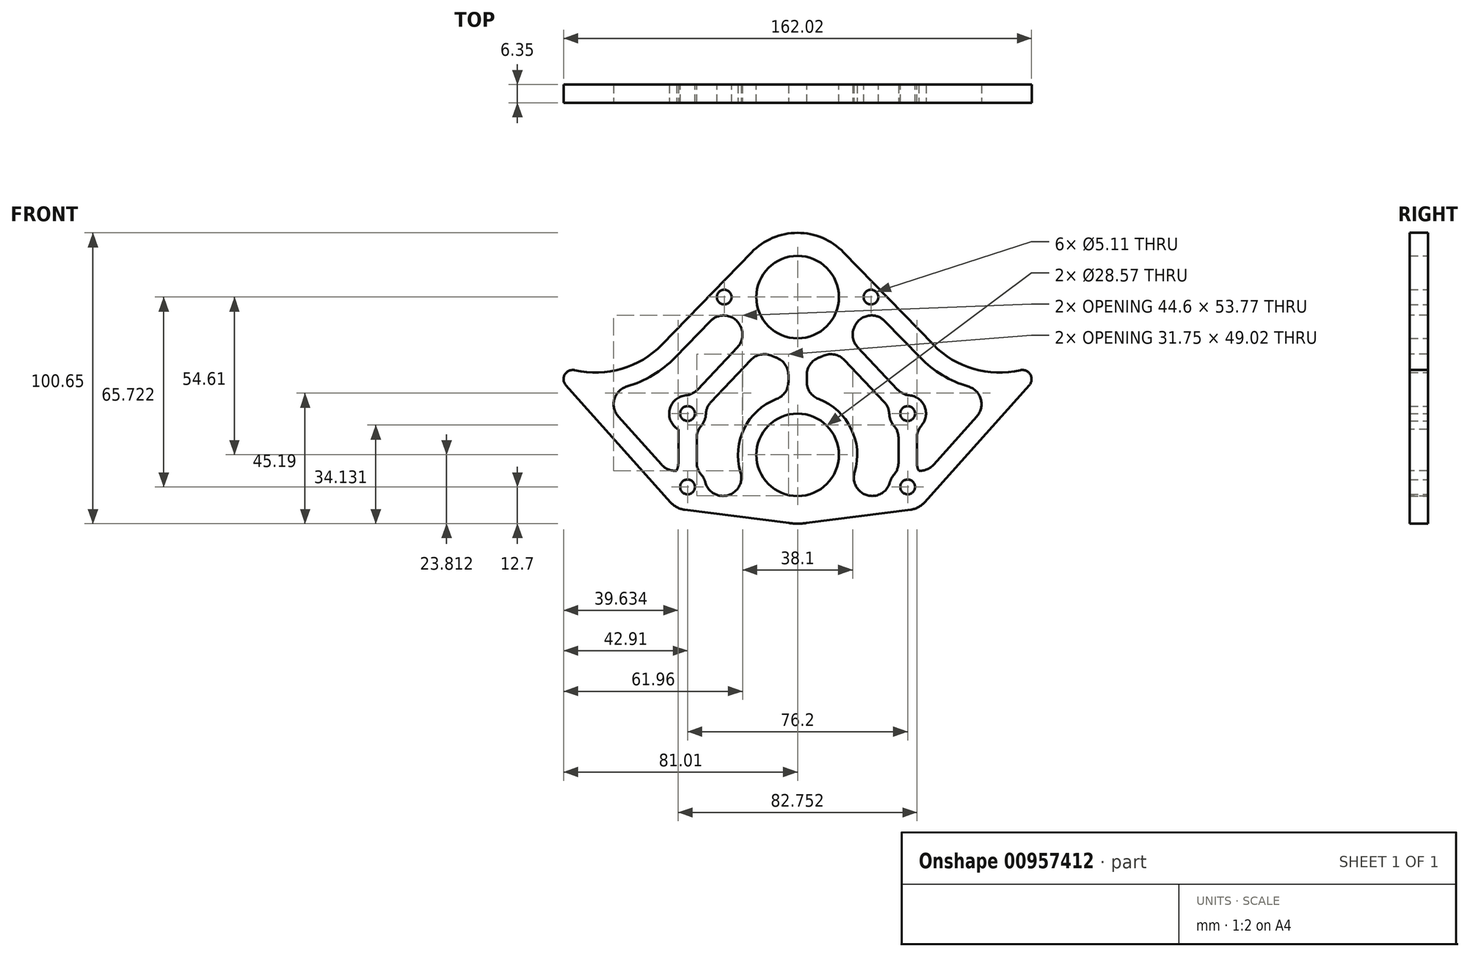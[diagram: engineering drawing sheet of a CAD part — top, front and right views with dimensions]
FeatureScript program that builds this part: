
annotation { "Feature Type Name" : "Feature", "Feature Type Description" : "" }
export const myFeature = defineFeature(function(context is Context, id is Id, definition is map)
    precondition{}
    {
        {
            var Q0;
            Q0=qCreatedBy(makeId("Front.planeOp"),FACE);
            var sketch = newSketch(context, id + "F0", { "sketchPlane" : qUnion([Q0])});
            skCircle(sketch, "E0", {"center": v(-69.85, 58.74) * mm, "radius": 31.88 * mm, "construction": true});
            skCircle(sketch, "E1", {"center": v(69.85, 58.74) * mm, "radius": 31.88 * mm, "construction": true});
            skLineSegment(sketch, "E2", {"start": v(-69.85, 58.74) * mm, "end": v(69.85, 58.74) * mm, "construction": true});
            skLineSegment(sketch, "E3", {"start": v(0, 58.74) * mm, "end": v(0, 0) * mm, "construction": true});
            skLineSegment(sketch, "E4.bottom", {"start": v(-101.6, -25.4) * mm, "end": v(101.6, -25.4) * mm, "construction": true});
            skLineSegment(sketch, "E4.top", {"start": v(-101.6, 25.4) * mm, "end": v(101.6, 25.4) * mm, "construction": true});
            skLineSegment(sketch, "E4.left", {"start": v(-101.6, -25.4) * mm, "end": v(-101.6, 25.4) * mm, "construction": true});
            skLineSegment(sketch, "E4.right", {"start": v(101.6, -25.4) * mm, "end": v(101.6, 25.4) * mm, "construction": true});
            skPoint(sketch, "E4.middle", {"position": v(0, 0) * mm});
            skCircle(sketch, "E5", {"center": v(0, -1.59) * mm, "radius": 50.8 * mm, "construction": true});
            skCircle(sketch, "E6", {"center": v(-69.85, 58.74) * mm, "radius": 7.62 * mm, "construction": true});
            skCircle(sketch, "E7", {"center": v(69.85, 58.74) * mm, "radius": 7.62 * mm, "construction": true});
            skCircle(sketch, "E8", {"center": v(0, 53.02) * mm, "radius": 38.1 * mm, "construction": true});
            skCircle(sketch, "E9", {"center": v(0, 53.02) * mm, "radius": 27.94 * mm, "construction": true});
            skCircle(sketch, "E10", {"center": v(0, -1.59) * mm, "radius": 26.67 * mm, "construction": true});
            skCircle(sketch, "E11", {"center": v(0, 53.02) * mm, "radius": 19.05 * mm, "construction": true});
            skCircle(sketch, "E12", {"center": v(0, -1.59) * mm, "radius": 35.56 * mm, "construction": true});
            skCircle(sketch, "E13", {"center": v(-69.85, 58.74) * mm, "radius": 8.9 * mm, "construction": true});
            skCircle(sketch, "E14", {"center": v(69.85, 58.74) * mm, "radius": 8.9 * mm, "construction": true});
            skCircle(sketch, "E15", {"center": v(0, 53.02) * mm, "radius": 14.29 * mm});
            skCircle(sketch, "E16", {"center": v(0, -1.59) * mm, "radius": 14.29 * mm});
            skCircle(sketch, "E17", {"center": v(-88.9, 12.7) * mm, "radius": 2.55 * mm, "construction": true});
            skCircle(sketch, "E18.0.1.0", {"center": v(-88.9, -12.7) * mm, "radius": 2.55 * mm, "construction": true});
            skCircle(sketch, "E18.1.0.0", {"center": v(-63.5, 12.7) * mm, "radius": 2.55 * mm, "construction": true});
            skCircle(sketch, "E18.1.1.0", {"center": v(-63.5, -12.7) * mm, "radius": 2.55 * mm, "construction": true});
            skCircle(sketch, "E18.2.0.0", {"center": v(-38.1, 12.7) * mm, "radius": 2.55 * mm});
            skCircle(sketch, "E18.2.1.0", {"center": v(-38.1, -12.7) * mm, "radius": 2.55 * mm});
            skCircle(sketch, "E18.3.0.0", {"center": v(-12.7, 12.7) * mm, "radius": 2.55 * mm, "construction": true});
            skCircle(sketch, "E18.3.1.0", {"center": v(-12.7, -12.7) * mm, "radius": 2.55 * mm, "construction": true});
            skCircle(sketch, "E18.4.0.0", {"center": v(12.7, 12.7) * mm, "radius": 2.55 * mm, "construction": true});
            skCircle(sketch, "E18.4.1.0", {"center": v(12.7, -12.7) * mm, "radius": 2.55 * mm, "construction": true});
            skCircle(sketch, "E18.5.0.0", {"center": v(38.1, 12.7) * mm, "radius": 2.55 * mm});
            skCircle(sketch, "E18.5.1.0", {"center": v(38.1, -12.7) * mm, "radius": 2.55 * mm});
            skCircle(sketch, "E18.6.0.0", {"center": v(63.5, 12.7) * mm, "radius": 2.55 * mm, "construction": true});
            skCircle(sketch, "E18.6.1.0", {"center": v(63.5, -12.7) * mm, "radius": 2.55 * mm, "construction": true});
            skCircle(sketch, "E18.7.0.0", {"center": v(88.9, 12.7) * mm, "radius": 2.55 * mm, "construction": true});
            skCircle(sketch, "E18.7.1.0", {"center": v(88.9, -12.7) * mm, "radius": 2.55 * mm, "construction": true});
            skLineSegment(sketch, "E18.direction1", {"start": v(-88.9, 12.7) * mm, "end": v(-63.5, 12.7) * mm, "construction": true});
            skLineSegment(sketch, "E18.direction2", {"start": v(-88.9, 12.7) * mm, "end": v(-88.9, -12.7) * mm, "construction": true});
            skArc(sketch, "E19", {"start": v(-93.62, 37.5) * mm, "mid": v(-98.95, 71.76) * mm, "end": v(-69.85, 90.61) * mm, "construction": true});
            skLineSegment(sketch, "E20", {"start": v(-69.85, 90.61) * mm, "end": v(69.85, 90.61) * mm, "construction": true});
            skArc(sketch, "E21", {"start": v(69.85, 90.61) * mm, "mid": v(98.95, 71.76) * mm, "end": v(93.62, 37.5) * mm, "construction": true});
            skCircle(sketch, "E22", {"center": v(-69.85, 58.74) * mm, "radius": 9.55 * mm, "construction": true});
            skCircle(sketch, "E23", {"center": v(69.85, 58.74) * mm, "radius": 9.55 * mm, "construction": true});
            skLineSegment(sketch, "E24", {"start": v(-67.64, 84.04) * mm, "end": v(-69.85, 58.74) * mm, "construction": true});
            skLineSegment(sketch, "E25", {"start": v(-69.85, 58.74) * mm, "end": v(-72.06, 33.43) * mm, "construction": true});
            skCircle(sketch, "E26", {"center": v(-72.06, 33.43) * mm, "radius": 2.55 * mm, "construction": true});
            skCircle(sketch, "E27", {"center": v(-67.64, 84.04) * mm, "radius": 2.55 * mm, "construction": true});
            skCircle(sketch, "E28.MirrorC", {"center": v(72.06, 33.43) * mm, "radius": 2.55 * mm, "construction": true});
            skLineSegment(sketch, "E29.MirrorCS", {"start": v(69.85, 58.74) * mm, "end": v(72.06, 33.43) * mm, "construction": true});
            skLineSegment(sketch, "E30.MirrorCS", {"start": v(67.64, 84.04) * mm, "end": v(69.85, 58.74) * mm, "construction": true});
            skCircle(sketch, "E31.MirrorC", {"center": v(67.64, 84.04) * mm, "radius": 2.55 * mm, "construction": true});
            skCircle(sketch, "E32", {"center": v(0, -1.59) * mm, "radius": 23.81 * mm, "construction": true});
            skArc(sketch, "E33", {"start": v(3.03, -25.2) * mm, "mid": v(0, -25.4) * mm, "end": v(-3.03, -25.2) * mm});
            skCircle(sketch, "E34", {"center": v(-38.1, -12.7) * mm, "radius": 7.94 * mm, "construction": true});
            skCircle(sketch, "E35", {"center": v(38.1, -12.7) * mm, "radius": 7.94 * mm, "construction": true});
            skLineSegment(sketch, "E36", {"start": v(-3.03, -25.2) * mm, "end": v(-39.11, -20.57) * mm});
            skArc(sketch, "E37", {"start": v(-39.11, -20.57) * mm, "mid": v(-41.8, -19.72) * mm, "end": v(-44.02, -18) * mm});
            skLineSegment(sketch, "E38", {"start": v(-44.02, -18) * mm, "end": v(-80.2, 22.5) * mm});
            skLineSegment(sketch, "E39", {"start": v(3.03, -25.2) * mm, "end": v(39.11, -20.57) * mm});
            skArc(sketch, "E40", {"start": v(39.11, -20.57) * mm, "mid": v(41.8, -19.72) * mm, "end": v(44.02, -18) * mm});
            skLineSegment(sketch, "E41", {"start": v(44.02, -18) * mm, "end": v(80.2, 22.5) * mm});
            skCircle(sketch, "E42", {"center": v(-51.03, 75.8) * mm, "radius": 17.78 * mm, "construction": true});
            skCircle(sketch, "E43", {"center": v(-53.69, 37.52) * mm, "radius": 17.78 * mm, "construction": true});
            skCircle(sketch, "E44", {"center": v(51.03, 75.8) * mm, "radius": 17.78 * mm, "construction": true});
            skCircle(sketch, "E45", {"center": v(53.69, 37.52) * mm, "radius": 17.78 * mm, "construction": true});
            skCircle(sketch, "E46", {"center": v(-51.03, 75.8) * mm, "radius": 11.11 * mm, "construction": true});
            skCircle(sketch, "E47", {"center": v(-53.69, 37.52) * mm, "radius": 11.11 * mm, "construction": true});
            skCircle(sketch, "E48", {"center": v(53.69, 37.52) * mm, "radius": 11.11 * mm, "construction": true});
            skCircle(sketch, "E49", {"center": v(51.03, 75.8) * mm, "radius": 11.11 * mm, "construction": true});
            skCircle(sketch, "E50", {"center": v(0, 53.02) * mm, "radius": 22.23 * mm, "construction": true});
            skArc(sketch, "E51", {"start": v(-77.12, 27.7) * mm, "mid": v(-60.88, 28.15) * mm, "end": v(-46.98, 36.54) * mm});
            skLineSegment(sketch, "E52", {"start": v(-46.98, 36.54) * mm, "end": v(-15.95, 68.5) * mm});
            skArc(sketch, "E53", {"start": v(15.95, 68.5) * mm, "mid": v(0, 75.25) * mm, "end": v(-15.95, 68.5) * mm});
            skArc(sketch, "E54", {"start": v(46.98, 36.54) * mm, "mid": v(60.88, 28.15) * mm, "end": v(77.12, 27.7) * mm});
            skLineSegment(sketch, "E55", {"start": v(46.98, 36.54) * mm, "end": v(15.95, 68.5) * mm});
            skPoint(sketch, "E56.visualSharp", {"position": v(-93.62, 37.5) * mm});
            skArc(sketch, "E56.filletArc", {"start": v(-77.12, 27.7) * mm, "mid": v(-80.57, 26.23) * mm, "end": v(-80.2, 22.5) * mm});
            skPoint(sketch, "E57.visualSharp", {"position": v(93.62, 37.5) * mm});
            skArc(sketch, "E57.filletArc", {"start": v(80.2, 22.5) * mm, "mid": v(80.57, 26.23) * mm, "end": v(77.12, 27.7) * mm});
            skLineSegment(sketch, "E58", {"start": v(25.4, 53.02) * mm, "end": v(0, 53.02) * mm, "construction": true});
            skLineSegment(sketch, "E59", {"start": v(0, 53.02) * mm, "end": v(-25.4, 53.02) * mm, "construction": true});
            skCircle(sketch, "E60", {"center": v(-25.4, 53.02) * mm, "radius": 2.55 * mm});
            skCircle(sketch, "E61", {"center": v(25.4, 53.02) * mm, "radius": 2.55 * mm});
            skSolve(sketch);
        }
        {
            var Q0;
            Q0=qSketchRegion(id+"F0",true);
            extrude(context, id + "F1", {"entities" : qUnion([Q0]), "depth" : 6.35 * mm, "offsetDistance" : 25.4 * mm});
        }
        {
            var Q0;
            Q0=makeQuery(id+"F1.opExtrude","CAP_FACE",FACE,{"disambiguationData":[OSD([sQuery(id+"F0.wireOp",EDGE,"E15"),sQuery(id+"F0.wireOp",EDGE,"E16"),sQuery(id+"F0.wireOp",EDGE,"E18.2.0.0"),sQuery(id+"F0.wireOp",EDGE,"E18.2.1.0"),sQuery(id+"F0.wireOp",EDGE,"E18.5.0.0"),sQuery(id+"F0.wireOp",EDGE,"E18.5.1.0"),sQuery(id+"F0.wireOp",EDGE,"E33"),sQuery(id+"F0.wireOp",EDGE,"E36"),sQuery(id+"F0.wireOp",EDGE,"E37"),sQuery(id+"F0.wireOp",EDGE,"E38"),sQuery(id+"F0.wireOp",EDGE,"E39"),sQuery(id+"F0.wireOp",EDGE,"E40"),sQuery(id+"F0.wireOp",EDGE,"E41"),sQuery(id+"F0.wireOp",EDGE,"E51"),sQuery(id+"F0.wireOp",EDGE,"E52"),sQuery(id+"F0.wireOp",EDGE,"E53"),sQuery(id+"F0.wireOp",EDGE,"E54"),sQuery(id+"F0.wireOp",EDGE,"E55"),sQuery(id+"F0.wireOp",EDGE,"E56.filletArc"),sQuery(id+"F0.wireOp",EDGE,"E57.filletArc"),sQuery(id+"F0.wireOp",EDGE,"E60"),sQuery(id+"F0.wireOp",EDGE,"E61")])],"isStart":false});
            var sketch = newSketch(context, id + "F2", { "sketchPlane" : qUnion([Q0])});
            skCircle(sketch, "E62", {"center": v(0, 53.02) * mm, "radius": 22.23 * mm, "construction": true});
            skCircle(sketch, "E63", {"center": v(25.4, 53.02) * mm, "radius": 6.35 * mm, "construction": true});
            skCircle(sketch, "E64", {"center": v(-25.4, 53.02) * mm, "radius": 6.35 * mm, "construction": true});
            skCircle(sketch, "E65", {"center": v(-38.1, 12.7) * mm, "radius": 6.35 * mm, "construction": true});
            skCircle(sketch, "E66", {"center": v(-38.1, -12.7) * mm, "radius": 6.35 * mm, "construction": true});
            skCircle(sketch, "E67", {"center": v(38.1, -12.7) * mm, "radius": 6.35 * mm, "construction": true});
            skCircle(sketch, "E68", {"center": v(38.1, 12.7) * mm, "radius": 6.35 * mm, "construction": true});
            skLineSegment(sketch, "E69", {"start": v(-38.1, -12.7) * mm, "end": v(-38.1, 12.7) * mm, "construction": true});
            skLineSegment(sketch, "E70", {"start": v(-41.27, -7.2) * mm, "end": v(-41.27, 7.2) * mm});
            skLineSegment(sketch, "E71", {"start": v(-34.92, -7.2) * mm, "end": v(-34.92, 7.2) * mm});
            skCircle(sketch, "E72", {"center": v(0, -1.59) * mm, "radius": 20.64 * mm, "construction": true});
            skLineSegment(sketch, "E73", {"start": v(0, -1.59) * mm, "end": v(0, 53.02) * mm, "construction": true});
            skLineSegment(sketch, "E74", {"start": v(-3.18, 18.8) * mm, "end": v(-3.18, 31.03) * mm});
            skLineSegment(sketch, "E75", {"start": v(0, 53.02) * mm, "end": v(-38.1, 12.7) * mm, "construction": true});
            skLineSegment(sketch, "E76", {"start": v(-32.02, 14.52) * mm, "end": v(-12.8, 34.85) * mm});
            skArc(sketch, "E77.0", {"start": v(-38.3, -14.27) * mm, "mid": v(-38.84, -14.1) * mm, "end": v(-39.28, -13.76) * mm, "construction": true});
            skLineSegment(sketch, "E77.1", {"start": v(42.42, 32.11) * mm, "end": v(11.4, 64.08) * mm, "construction": true});
            skArc(sketch, "E77.2", {"start": v(11.4, 64.08) * mm, "mid": v(0, 68.9) * mm, "end": v(-11.4, 64.08) * mm, "construction": true});
            skLineSegment(sketch, "E77.3", {"start": v(-42.42, 32.11) * mm, "end": v(-11.4, 64.08) * mm, "construction": true});
            skArc(sketch, "E77.4", {"start": v(-69.92, 20.51) * mm, "mid": v(-54.99, 23.52) * mm, "end": v(-42.42, 32.11) * mm});
            skArc(sketch, "E77.5", {"start": v(42.42, 32.11) * mm, "mid": v(54.99, 23.52) * mm, "end": v(69.92, 20.51) * mm, "construction": true});
            skLineSegment(sketch, "E77.6", {"start": v(-39.28, -13.76) * mm, "end": v(-69.92, 20.51) * mm, "construction": true});
            skLineSegment(sketch, "E77.7", {"start": v(39.28, -13.76) * mm, "end": v(69.92, 20.51) * mm, "construction": true});
            skArc(sketch, "E77.8", {"start": v(38.3, -14.27) * mm, "mid": v(38.84, -14.1) * mm, "end": v(39.28, -13.76) * mm, "construction": true});
            skLineSegment(sketch, "E77.9", {"start": v(2.22, -18.9) * mm, "end": v(38.3, -14.27) * mm, "construction": true});
            skArc(sketch, "E77.10", {"start": v(2.22, -18.9) * mm, "mid": v(0, -19.05) * mm, "end": v(-2.22, -18.9) * mm, "construction": true});
            skLineSegment(sketch, "E77.11", {"start": v(-2.22, -18.9) * mm, "end": v(-38.3, -14.27) * mm, "construction": true});
            skArc(sketch, "E78", {"start": v(-32.2, -15.06) * mm, "mid": v(-32.1, -10.62) * mm, "end": v(-34.92, -7.2) * mm});
            skArc(sketch, "E79", {"start": v(-3.18, 18.8) * mm, "mid": v(-19.9, 3.87) * mm, "end": v(-13.13, -17.5) * mm});
            skLineSegment(sketch, "E80", {"start": v(-13.13, -17.5) * mm, "end": v(-32.2, -15.06) * mm});
            skArc(sketch, "E81", {"start": v(-32.02, 14.52) * mm, "mid": v(-32.2, 10.35) * mm, "end": v(-34.92, 7.2) * mm});
            skArc(sketch, "E82", {"start": v(-12.8, 34.85) * mm, "mid": v(-8.21, 32.37) * mm, "end": v(-3.17, 31.03) * mm});
            skLineSegment(sketch, "E83", {"start": v(-36.63, 18.88) * mm, "end": v(-17.42, 39.21) * mm});
            skArc(sketch, "E84", {"start": v(-41.27, 7.2) * mm, "mid": v(-44, 15.05) * mm, "end": v(-36.63, 18.88) * mm});
            skArc(sketch, "E85", {"start": v(-17.42, 39.21) * mm, "mid": v(-20, 43.33) * mm, "end": v(-21.63, 47.91) * mm});
            skArc(sketch, "E86", {"start": v(-27.82, 47.15) * mm, "mid": v(-24.63, 46.72) * mm, "end": v(-21.63, 47.91) * mm});
            skLineSegment(sketch, "E87", {"start": v(-42.42, 32.11) * mm, "end": v(-27.82, 47.15) * mm});
            skLineSegment(sketch, "E88", {"start": v(-43.38, -9.17) * mm, "end": v(-69.92, 20.51) * mm});
            skArc(sketch, "E89", {"start": v(-41.27, -7.2) * mm, "mid": v(-42.44, -8.07) * mm, "end": v(-43.38, -9.17) * mm});
            skArc(sketch, "E90.MirrorCS", {"start": v(41.27, -7.2) * mm, "mid": v(42.44, -8.07) * mm, "end": v(43.38, -9.17) * mm});
            skArc(sketch, "E91.MirrorCS", {"start": v(27.82, 47.15) * mm, "mid": v(24.63, 46.72) * mm, "end": v(21.63, 47.91) * mm});
            skArc(sketch, "E92.MirrorCS", {"start": v(32.2, -15.06) * mm, "mid": v(32.1, -10.62) * mm, "end": v(34.92, -7.2) * mm});
            skLineSegment(sketch, "E93.MirrorCS", {"start": v(13.13, -17.5) * mm, "end": v(32.2, -15.06) * mm});
            skLineSegment(sketch, "E94.MirrorCS", {"start": v(43.38, -9.17) * mm, "end": v(69.92, 20.51) * mm});
            skArc(sketch, "E95.MirrorCS", {"start": v(41.27, 7.2) * mm, "mid": v(44, 15.05) * mm, "end": v(36.63, 18.88) * mm});
            skArc(sketch, "E96.MirrorCS", {"start": v(32.02, 14.52) * mm, "mid": v(32.2, 10.35) * mm, "end": v(34.92, 7.2) * mm});
            skLineSegment(sketch, "E97.MirrorCS", {"start": v(42.42, 32.11) * mm, "end": v(27.82, 47.15) * mm});
            skLineSegment(sketch, "E98.MirrorCS", {"start": v(32.02, 14.52) * mm, "end": v(12.8, 34.85) * mm});
            skLineSegment(sketch, "E99.MirrorCS", {"start": v(3.18, 18.8) * mm, "end": v(3.18, 31.03) * mm});
            skArc(sketch, "E100.MirrorCS", {"start": v(69.92, 20.51) * mm, "mid": v(54.99, 23.52) * mm, "end": v(42.42, 32.11) * mm});
            skLineSegment(sketch, "E101.MirrorCS", {"start": v(41.27, -7.2) * mm, "end": v(41.27, 7.2) * mm});
            skLineSegment(sketch, "E102.MirrorCS", {"start": v(0, 53.02) * mm, "end": v(38.1, 12.7) * mm, "construction": true});
            skLineSegment(sketch, "E103.MirrorCS", {"start": v(34.92, -7.2) * mm, "end": v(34.92, 7.2) * mm});
            skArc(sketch, "E104.MirrorCS", {"start": v(17.42, 39.21) * mm, "mid": v(20, 43.33) * mm, "end": v(21.63, 47.91) * mm});
            skArc(sketch, "E105.MirrorCS", {"start": v(-2.22, -18.9) * mm, "mid": v(0, -19.05) * mm, "end": v(2.22, -18.9) * mm, "construction": true});
            skArc(sketch, "E106.MirrorCS", {"start": v(3.18, 18.8) * mm, "mid": v(19.9, 3.87) * mm, "end": v(13.13, -17.5) * mm});
            skLineSegment(sketch, "E107.MirrorCS", {"start": v(38.1, -12.7) * mm, "end": v(38.1, 12.7) * mm, "construction": true});
            skArc(sketch, "E108.MirrorCS", {"start": v(12.8, 34.85) * mm, "mid": v(8.21, 32.37) * mm, "end": v(3.17, 31.03) * mm});
            skLineSegment(sketch, "E109.MirrorCS", {"start": v(36.63, 18.88) * mm, "end": v(17.42, 39.21) * mm});
            skSolve(sketch);
        }
        {
            var Q0;
            Q0 = qSketchRegion(id + "F2", true);
            extrude(context, id + "F3", {"entities" : qUnion([Q0]), "operationType" : NewBodyOperationType.REMOVE, "oppositeDirection" : true, "depth" : 25.4 * mm, "offsetDistance" : 25.4 * mm});
        }
        {
            var Q0;
            Q0=makeQuery(id+"F3.boolean.opBoolean","COPY",EDGE,{"derivedFrom":makeQuery(id+"F3.opExtrude","SWEPT_EDGE",EDGE,{"disambiguationData":[OSD([sQuery(id+"F2.wireOp",EDGE,"E86"),sQuery(id+"F2.wireOp",EDGE,"E87")])]})});
            var Q1;
            Q1=makeQuery(id+"F3.boolean.opBoolean","COPY",EDGE,{"derivedFrom":makeQuery(id+"F3.opExtrude","SWEPT_EDGE",EDGE,{"disambiguationData":[OSD([sQuery(id+"F2.wireOp",EDGE,"E85"),sQuery(id+"F2.wireOp",EDGE,"E86")])]})});
            var Q2;
            Q2=makeQuery(id+"F3.boolean.opBoolean","COPY",EDGE,{"derivedFrom":makeQuery(id+"F3.opExtrude","SWEPT_EDGE",EDGE,{"disambiguationData":[OSD([sQuery(id+"F2.wireOp",EDGE,"E83"),sQuery(id+"F2.wireOp",EDGE,"E85")])]})});
            var Q3;
            Q3=makeQuery(id+"F3.boolean.opBoolean","COPY",EDGE,{"derivedFrom":makeQuery(id+"F3.opExtrude","SWEPT_EDGE",EDGE,{"disambiguationData":[OSD([sQuery(id+"F2.wireOp",EDGE,"E74"),sQuery(id+"F2.wireOp",EDGE,"E79")])]})});
            var Q4;
            Q4=makeQuery(id+"F3.boolean.opBoolean","COPY",EDGE,{"derivedFrom":makeQuery(id+"F3.opExtrude","SWEPT_EDGE",EDGE,{"disambiguationData":[OSD([sQuery(id+"F2.wireOp",EDGE,"E83"),sQuery(id+"F2.wireOp",EDGE,"E84")])]})});
            var Q5;
            Q5=makeQuery(id+"F3.boolean.opBoolean","COPY",EDGE,{"derivedFrom":makeQuery(id+"F3.opExtrude","SWEPT_EDGE",EDGE,{"disambiguationData":[OSD([sQuery(id+"F2.wireOp",EDGE,"E70"),sQuery(id+"F2.wireOp",EDGE,"E89")])]})});
            var Q6;
            Q6=makeQuery(id+"F3.boolean.opBoolean","COPY",EDGE,{"derivedFrom":makeQuery(id+"F3.opExtrude","SWEPT_EDGE",EDGE,{"disambiguationData":[OSD([sQuery(id+"F2.wireOp",EDGE,"E88"),sQuery(id+"F2.wireOp",EDGE,"E89")])]})});
            var Q7;
            Q7=makeQuery(id+"F3.boolean.opBoolean","COPY",EDGE,{"derivedFrom":makeQuery(id+"F3.opExtrude","SWEPT_EDGE",EDGE,{"disambiguationData":[OSD([sQuery(id+"F2.wireOp",EDGE,"E77.4"),sQuery(id+"F2.wireOp",EDGE,"E88")])]})});
            var Q8;
            Q8=makeQuery(id+"F3.boolean.opBoolean","COPY",EDGE,{"derivedFrom":makeQuery(id+"F3.opExtrude","SWEPT_EDGE",EDGE,{"disambiguationData":[OSD([sQuery(id+"F2.wireOp",EDGE,"E71"),sQuery(id+"F2.wireOp",EDGE,"E78")])]})});
            var Q9;
            Q9=makeQuery(id+"F3.boolean.opBoolean","COPY",EDGE,{"derivedFrom":makeQuery(id+"F3.opExtrude","SWEPT_EDGE",EDGE,{"disambiguationData":[OSD([sQuery(id+"F2.wireOp",EDGE,"E71"),sQuery(id+"F2.wireOp",EDGE,"E81")])]})});
            var Q10;
            Q10=makeQuery(id+"F3.boolean.opBoolean","COPY",EDGE,{"derivedFrom":makeQuery(id+"F3.opExtrude","SWEPT_EDGE",EDGE,{"disambiguationData":[OSD([sQuery(id+"F2.wireOp",EDGE,"E76"),sQuery(id+"F2.wireOp",EDGE,"E81")])]})});
            var Q11;
            Q11=makeQuery(id+"F3.boolean.opBoolean","COPY",EDGE,{"derivedFrom":makeQuery(id+"F3.opExtrude","SWEPT_EDGE",EDGE,{"disambiguationData":[OSD([sQuery(id+"F2.wireOp",EDGE,"E78"),sQuery(id+"F2.wireOp",EDGE,"E80")])]})});
            var Q12;
            Q12=makeQuery(id+"F3.boolean.opBoolean","COPY",EDGE,{"derivedFrom":makeQuery(id+"F3.opExtrude","SWEPT_EDGE",EDGE,{"disambiguationData":[OSD([sQuery(id+"F2.wireOp",EDGE,"E99.MirrorCS"),sQuery(id+"F2.wireOp",EDGE,"E106.MirrorCS")])]})});
            var Q13;
            Q13=makeQuery(id+"F3.boolean.opBoolean","COPY",EDGE,{"derivedFrom":makeQuery(id+"F3.opExtrude","SWEPT_EDGE",EDGE,{"disambiguationData":[OSD([sQuery(id+"F2.wireOp",EDGE,"E79"),sQuery(id+"F2.wireOp",EDGE,"E80")])]})});
            var Q14;
            Q14=makeQuery(id+"F3.boolean.opBoolean","COPY",EDGE,{"derivedFrom":makeQuery(id+"F3.opExtrude","SWEPT_EDGE",EDGE,{"disambiguationData":[OSD([sQuery(id+"F2.wireOp",EDGE,"E92.MirrorCS"),sQuery(id+"F2.wireOp",EDGE,"E93.MirrorCS")])]})});
            var Q15;
            Q15=makeQuery(id+"F3.boolean.opBoolean","COPY",EDGE,{"derivedFrom":makeQuery(id+"F3.opExtrude","SWEPT_EDGE",EDGE,{"disambiguationData":[OSD([sQuery(id+"F2.wireOp",EDGE,"E92.MirrorCS"),sQuery(id+"F2.wireOp",EDGE,"E103.MirrorCS")])]})});
            var Q16;
            Q16=makeQuery(id+"F3.boolean.opBoolean","COPY",EDGE,{"derivedFrom":makeQuery(id+"F3.opExtrude","SWEPT_EDGE",EDGE,{"disambiguationData":[OSD([sQuery(id+"F2.wireOp",EDGE,"E93.MirrorCS"),sQuery(id+"F2.wireOp",EDGE,"E106.MirrorCS")])]})});
            var Q17;
            Q17=makeQuery(id+"F3.boolean.opBoolean","COPY",EDGE,{"derivedFrom":makeQuery(id+"F3.opExtrude","SWEPT_EDGE",EDGE,{"disambiguationData":[OSD([sQuery(id+"F2.wireOp",EDGE,"E95.MirrorCS"),sQuery(id+"F2.wireOp",EDGE,"E109.MirrorCS")])]})});
            var Q18;
            Q18=makeQuery(id+"F3.boolean.opBoolean","COPY",EDGE,{"derivedFrom":makeQuery(id+"F3.opExtrude","SWEPT_EDGE",EDGE,{"disambiguationData":[OSD([sQuery(id+"F2.wireOp",EDGE,"E95.MirrorCS"),sQuery(id+"F2.wireOp",EDGE,"E101.MirrorCS")])]})});
            var Q19;
            Q19=makeQuery(id+"F3.boolean.opBoolean","COPY",EDGE,{"derivedFrom":makeQuery(id+"F3.opExtrude","SWEPT_EDGE",EDGE,{"disambiguationData":[OSD([sQuery(id+"F2.wireOp",EDGE,"E104.MirrorCS"),sQuery(id+"F2.wireOp",EDGE,"E109.MirrorCS")])]})});
            var Q20;
            Q20=makeQuery(id+"F3.boolean.opBoolean","COPY",EDGE,{"derivedFrom":makeQuery(id+"F3.opExtrude","SWEPT_EDGE",EDGE,{"disambiguationData":[OSD([sQuery(id+"F2.wireOp",EDGE,"E76"),sQuery(id+"F2.wireOp",EDGE,"E82")])]})});
            var Q21;
            Q21=makeQuery(id+"F3.boolean.opBoolean","COPY",EDGE,{"derivedFrom":makeQuery(id+"F3.opExtrude","SWEPT_EDGE",EDGE,{"disambiguationData":[OSD([sQuery(id+"F2.wireOp",EDGE,"E99.MirrorCS"),sQuery(id+"F2.wireOp",EDGE,"E108.MirrorCS")])]})});
            var Q22;
            Q22=makeQuery(id+"F3.boolean.opBoolean","COPY",EDGE,{"derivedFrom":makeQuery(id+"F3.opExtrude","SWEPT_EDGE",EDGE,{"disambiguationData":[OSD([sQuery(id+"F2.wireOp",EDGE,"E74"),sQuery(id+"F2.wireOp",EDGE,"E82")])]})});
            var Q23;
            Q23=makeQuery(id+"F3.boolean.opBoolean","COPY",EDGE,{"derivedFrom":makeQuery(id+"F3.opExtrude","SWEPT_EDGE",EDGE,{"disambiguationData":[OSD([sQuery(id+"F2.wireOp",EDGE,"E98.MirrorCS"),sQuery(id+"F2.wireOp",EDGE,"E108.MirrorCS")])]})});
            var Q24;
            Q24=makeQuery(id+"F3.boolean.opBoolean","COPY",EDGE,{"derivedFrom":makeQuery(id+"F3.opExtrude","SWEPT_EDGE",EDGE,{"disambiguationData":[OSD([sQuery(id+"F2.wireOp",EDGE,"E96.MirrorCS"),sQuery(id+"F2.wireOp",EDGE,"E98.MirrorCS")])]})});
            var Q25;
            Q25=makeQuery(id+"F3.boolean.opBoolean","COPY",EDGE,{"derivedFrom":makeQuery(id+"F3.opExtrude","SWEPT_EDGE",EDGE,{"disambiguationData":[OSD([sQuery(id+"F2.wireOp",EDGE,"E96.MirrorCS"),sQuery(id+"F2.wireOp",EDGE,"E103.MirrorCS")])]})});
            var Q26;
            Q26=makeQuery(id+"F3.boolean.opBoolean","COPY",EDGE,{"derivedFrom":makeQuery(id+"F3.opExtrude","SWEPT_EDGE",EDGE,{"disambiguationData":[OSD([sQuery(id+"F2.wireOp",EDGE,"E94.MirrorCS"),sQuery(id+"F2.wireOp",EDGE,"E100.MirrorCS")])]})});
            var Q27;
            Q27=makeQuery(id+"F3.boolean.opBoolean","COPY",EDGE,{"derivedFrom":makeQuery(id+"F3.opExtrude","SWEPT_EDGE",EDGE,{"disambiguationData":[OSD([sQuery(id+"F2.wireOp",EDGE,"E91.MirrorCS"),sQuery(id+"F2.wireOp",EDGE,"E104.MirrorCS")])]})});
            var Q28;
            Q28=makeQuery(id+"F3.boolean.opBoolean","COPY",EDGE,{"derivedFrom":makeQuery(id+"F3.opExtrude","SWEPT_EDGE",EDGE,{"disambiguationData":[OSD([sQuery(id+"F2.wireOp",EDGE,"E91.MirrorCS"),sQuery(id+"F2.wireOp",EDGE,"E97.MirrorCS")])]})});
            var Q29;
            Q29=makeQuery(id+"F3.boolean.opBoolean","COPY",EDGE,{"derivedFrom":makeQuery(id+"F3.opExtrude","SWEPT_EDGE",EDGE,{"disambiguationData":[OSD([sQuery(id+"F2.wireOp",EDGE,"E90.MirrorCS"),sQuery(id+"F2.wireOp",EDGE,"E101.MirrorCS")])]})});
            var Q30;
            Q30=makeQuery(id+"F3.boolean.opBoolean","COPY",EDGE,{"derivedFrom":makeQuery(id+"F3.opExtrude","SWEPT_EDGE",EDGE,{"disambiguationData":[OSD([sQuery(id+"F2.wireOp",EDGE,"E90.MirrorCS"),sQuery(id+"F2.wireOp",EDGE,"E94.MirrorCS")])]})});
            fillet(context, id + "F4", {"entities" : qUnion([Q0, Q1, Q2, Q3, Q4, Q5, Q6, Q7, Q8, Q9, Q10, Q11, Q12, Q13, Q14, Q15, Q16, Q17, Q18, Q19, Q20, Q21, Q22, Q23, Q24, Q25, Q26, Q27, Q28, Q29, Q30]), "radius" : 6.35 * mm, "tangentPropagation" : true, "allowEdgeOverflow" : false});
        }
    });
